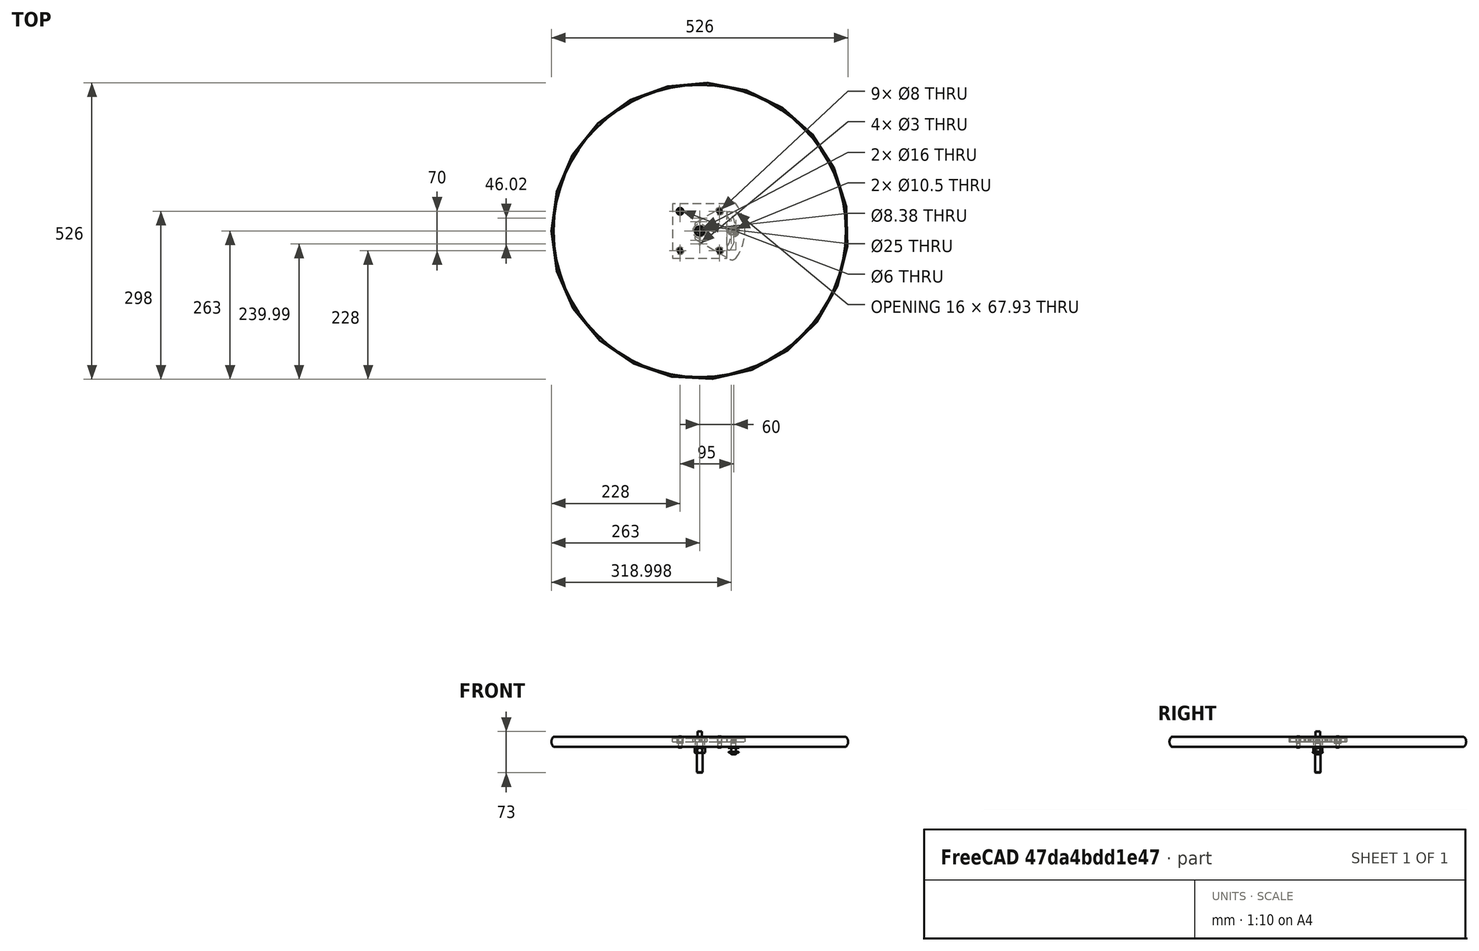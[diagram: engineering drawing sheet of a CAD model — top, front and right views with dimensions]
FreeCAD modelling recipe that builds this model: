
FCSTD DOCUMENT  (FreeCAD 0.19R24366 (Git))
Label: assembly
License: All rights reserved
LicenseURL: http://en.wikipedia.org/wiki/All_rights_reserved
objects: TechDraw::DrawViewDimension×16, Sketcher::SketchObject×14, Part::FeaturePython×13, PartDesign::Hole×8, App::FeaturePython×7, PartDesign::Body×6, App::Part×5, TechDraw::DrawViewPart×4, PartDesign::Revolution×3, PartDesign::Pad×3, PartDesign::Chamfer×1, TechDraw::DrawSVGTemplate×1, TechDraw::DrawRichAnno×1, TechDraw::DrawPage×1
note: 62 computed .brp shape members not serialized (recipe doc carries the construction recipe); baked Part::Feature solids carry a one-line shape summary decoded from their .brp

FEATURE [Sketcher::SketchObject] Sketch
  FullyConstrained = false
  MapMode = 5
  Placement = pos=(0,0,0) rot=(1,0,0;1.5708rad)
  Support = -> [XZ_Plane001]
  sketch-geometry (5):
    g0: LineSegment StartX=0 StartY=9 StartZ=0 EndX=-259 EndY=9 EndZ=0
    g1: LineSegment StartX=0 StartY=9 StartZ=0 EndX=0 EndY=-9 EndZ=0
    g2: LineSegment StartX=0 StartY=-9 StartZ=0 EndX=-259 EndY=-9 EndZ=0
    g3: ArcOfCircle CenterX=-250.875 CenterY=0 CenterZ=0 NormalX=0 NormalY=0 NormalZ=1 AngleXU=0 Radius=12.125 StartAngle=2.30514 EndAngle=3.97804
    g4: LineSegment StartX=-263 StartY=113.76 StartZ=0 EndX=-263 EndY=-132.948 EndZ=0
  constraints (14):
    c: PointOnObject(g0,g-2)
    c: Horizontal(g0)
    c: Coincident(g1,g0)
    c: Horizontal(g2)
    c: PointOnObject(g3,g-1)
    c: Coincident(g3,g0)
    c: Coincident(g3,g2)
    c: Symmetric(g1,g0,g-1)
    c: DistanceX(g0,g0) = 259
    c: Vertical(g4)
    c: DistanceX(g4,g-1) = 263
    c: Tangent(g3,g4)
    c: Coincident(g1,g2)
    c: DistanceY(g1,g1) = 18
FEATURE [PartDesign::Revolution] Revolution
  Angle = 360
  Axis = (0,2e-16,1)
  Base = (0,0,0)
  Placement = pos=(0,0,0) rot=(1,0,0;1.5708rad)
  Profile = -> Sketch
  ReferenceAxis = -> Sketch [V_Axis]
FEATURE [Sketcher::SketchObject] Sketch001
  FullyConstrained = false
  MapMode = 5
  Placement = pos=(0,4e-15,9) rot=(0,0,1;3.14159rad)
  Support = -> [Revolution]
  sketch-geometry (1):
    g0: Circle CenterX=0 CenterY=0 CenterZ=0 NormalX=0 NormalY=0 NormalZ=1 AngleXU=0 Radius=3.02563
  constraints (1):
    c: Coincident(g0,g-1)
FEATURE [PartDesign::Hole] Hole
  BaseFeature = -> Revolution
  Depth = 25
  DepthType = 0
  Diameter = 16
  DrillForDepth = false
  DrillPoint = 1
  DrillPointAngle = 118
  HoleCutCountersinkAngle = 90
  HoleCutCustomValues = false
  HoleCutDepth = 0
  HoleCutDiameter = 6.1
  HoleCutType = 0
  ModelActualThread = false
  Placement = pos=(0,0,0) rot=(1,0,0;1.5708rad)
  Profile = -> Sketch001
  Tapered = false
  TaperedAngle = 90
  ThreadAngle = 0
  ThreadClass = 0
  ThreadCutOffInner = 0
  ThreadCutOffOuter = 0
  ThreadDirection = 0
  ThreadFit = 0
  ThreadPitch = 0
  ThreadSize = 0
  ThreadType = 0
  Threaded = false
FEATURE [Sketcher::SketchObject] Sketch002
  FullyConstrained = true
  MapMode = 5
  Support = -> [XY_Plane003]
  sketch-geometry (4):
    g0: LineSegment StartX=-48.5 StartY=-48.5 StartZ=0 EndX=48.5 EndY=-48.5 EndZ=0
    g1: LineSegment StartX=48.5 StartY=-48.5 StartZ=0 EndX=48.5 EndY=48.5 EndZ=0
    g2: LineSegment StartX=48.5 StartY=48.5 StartZ=0 EndX=-48.5 EndY=48.5 EndZ=0
    g3: LineSegment StartX=-48.5 StartY=48.5 StartZ=0 EndX=-48.5 EndY=-48.5 EndZ=0
  constraints (11):
    c: Coincident(g0,g1)
    c: Coincident(g1,g2)
    c: Coincident(g2,g3)
    c: Coincident(g3,g0)
    c: Horizontal(g0)
    c: Horizontal(g2)
    c: Vertical(g1)
    c: Vertical(g3)
    c: Symmetric(g2,g0,g-1)
    c: Equal(g2,g1)
    c: DistanceX(g2,g2) = 97
FEATURE [PartDesign::Pad] Pad
  Direction = (1,1,1)
  Length = 6
  Length2 = 100
  Profile = -> Sketch002
  Type = 0
FEATURE [Sketcher::SketchObject] Sketch003
  FullyConstrained = false
  MapMode = 5
  Placement = pos=(0,0,6) rot=(0,0,1;0rad)
  Support = -> [Pad]
  sketch-geometry (6):
    g0: Circle CenterX=35 CenterY=35 CenterZ=0 NormalX=0 NormalY=0 NormalZ=1 AngleXU=0 Radius=3.3
    g1: Circle CenterX=35 CenterY=-35 CenterZ=0 NormalX=0 NormalY=0 NormalZ=1 AngleXU=0 Radius=3.3
    g2: Circle CenterX=-35 CenterY=35 CenterZ=0 NormalX=0 NormalY=0 NormalZ=1 AngleXU=0 Radius=3.3
    g3: Circle CenterX=-35 CenterY=-35 CenterZ=0 NormalX=0 NormalY=0 NormalZ=1 AngleXU=0 Radius=3.3
    g4: LineSegment StartX=-35 StartY=35 StartZ=0 EndX=35 EndY=35 EndZ=0
    g5: LineSegment StartX=35 StartY=35 StartZ=0 EndX=35 EndY=-35 EndZ=0
  constraints (9):
    c: Symmetric(g1,g2,g-1)
    c: Symmetric(g0,g3,g-1)
    c: Symmetric(g2,g0,g-2)
    c: Coincident(g4,g2)
    c: Coincident(g4,g0)
    c: DistanceX(g4,g4) = 70
    c: Coincident(g5,g4)
    c: Coincident(g5,g1)
    c: Equal(g4,g5)
FEATURE [PartDesign::Hole] Hole001
  BaseFeature = -> Pad
  Depth = 25
  DepthType = 0
  Diameter = 8
  DrillForDepth = false
  DrillPoint = 1
  DrillPointAngle = 118
  HoleCutCountersinkAngle = 90
  HoleCutCustomValues = false
  HoleCutDepth = 0
  HoleCutDiameter = 0
  HoleCutType = 0
  ModelActualThread = false
  Profile = -> Sketch003
  Tapered = false
  TaperedAngle = 90
  ThreadAngle = 0
  ThreadClass = 0
  ThreadCutOffInner = 0
  ThreadCutOffOuter = 0
  ThreadDirection = 0
  ThreadFit = 0
  ThreadPitch = 0
  ThreadSize = 0
  ThreadType = 0
  Threaded = false
FEATURE [Sketcher::SketchObject] Sketch004
  FullyConstrained = false
  MapMode = 5
  Placement = pos=(0,0,6) rot=(0,0,1;0rad)
  Support = -> [Hole001]
  sketch-geometry (1):
    g0: Circle CenterX=0 CenterY=0 CenterZ=0 NormalX=0 NormalY=0 NormalZ=1 AngleXU=0 Radius=7.11938
  constraints (1):
    c: Coincident(g0,g-1)
FEATURE [PartDesign::Hole] Hole002
  BaseFeature = -> Hole001
  Depth = 25
  DepthType = 0
  Diameter = 25
  DrillForDepth = false
  DrillPoint = 1
  DrillPointAngle = 118
  HoleCutCountersinkAngle = 90
  HoleCutCustomValues = false
  HoleCutDepth = 0
  HoleCutDiameter = 6.1
  HoleCutType = 0
  ModelActualThread = false
  Profile = -> Sketch004
  Tapered = false
  TaperedAngle = 90
  ThreadAngle = 0
  ThreadClass = 0
  ThreadCutOffInner = 0
  ThreadCutOffOuter = 0
  ThreadDirection = 0
  ThreadFit = 0
  ThreadPitch = 0
  ThreadSize = 0
  ThreadType = 0
  Threaded = false
  expr: Diameter = 2 * Sketch010.Constraints[16]
FEATURE [Sketcher::SketchObject] Sketch005
  FullyConstrained = false
  MapMode = 5
  Placement = pos=(0,0,6) rot=(0,0,1;0rad)
  Support = -> [Hole002]
  sketch-geometry (6):
    g0: Circle CenterX=0 CenterY=16.22 CenterZ=0 NormalX=0 NormalY=0 NormalZ=1 AngleXU=0 Radius=1.5917
    g1: Circle CenterX=0 CenterY=23.01 CenterZ=0 NormalX=0 NormalY=0 NormalZ=1 AngleXU=0 Radius=1.57748
    g2: Circle CenterX=0 CenterY=-16.22 CenterZ=0 NormalX=0 NormalY=0 NormalZ=1 AngleXU=0 Radius=1.5917
    g3: Circle CenterX=0 CenterY=-23.01 CenterZ=0 NormalX=0 NormalY=0 NormalZ=1 AngleXU=0 Radius=1.66102
    g4: Circle CenterX=0 CenterY=0 CenterZ=0 NormalX=0 NormalY=0 NormalZ=1 AngleXU=0 Radius=23.01
    g5: Circle CenterX=0 CenterY=0 CenterZ=0 NormalX=0 NormalY=0 NormalZ=1 AngleXU=0 Radius=16.22
  constraints (10):
    c: PointOnObject(g0,g-2)
    c: PointOnObject(g1,g-2)
    c: Symmetric(g0,g2,g-1)
    c: Symmetric(g3,g1,g-1)
    c: Coincident(g4,g-1)
    c: Diameter(g4) = 46.02
    c: PointOnObject(g1,g4)
    c: Coincident(g5,g-1)
    c: Diameter(g5) = 32.44
    c: PointOnObject(g0,g5)
FEATURE [PartDesign::Hole] Hole003
  BaseFeature = -> Hole002
  Depth = 25
  DepthType = 0
  Diameter = 3
  DrillForDepth = false
  DrillPoint = 1
  DrillPointAngle = 118
  HoleCutCountersinkAngle = 90
  HoleCutCustomValues = false
  HoleCutDepth = 0
  HoleCutDiameter = 6.1
  HoleCutType = 0
  ModelActualThread = false
  Profile = -> Sketch005
  Tapered = false
  TaperedAngle = 90
  ThreadAngle = 0
  ThreadClass = 0
  ThreadCutOffInner = 0
  ThreadCutOffOuter = 0
  ThreadDirection = 0
  ThreadFit = 0
  ThreadPitch = 0
  ThreadSize = 0
  ThreadType = 0
  Threaded = false
FEATURE [PartDesign::Body] Body001
  Group = -> [Sketch002,Pad,Sketch003,Hole001,Sketch004,Hole002,Sketch005,Hole003]
  Origin = -> Origin003
  Tip = -> Hole003
FEATURE [Sketcher::SketchObject] Sketch007
  FullyConstrained = false
  MapMode = 5
  Placement = pos=(0,0,0) rot=(1,0,0;1.5708rad)
  Support = -> [XZ_Plane005]
  sketch-geometry (5):
    g0: LineSegment StartX=0 StartY=9 StartZ=0 EndX=-259 EndY=9 EndZ=0
    g1: LineSegment StartX=0 StartY=9 StartZ=0 EndX=0 EndY=-9 EndZ=0
    g2: LineSegment StartX=0 StartY=-9 StartZ=0 EndX=-259 EndY=-9 EndZ=0
    g3: ArcOfCircle CenterX=-250.875 CenterY=0 CenterZ=0 NormalX=0 NormalY=0 NormalZ=1 AngleXU=0 Radius=12.125 StartAngle=2.30514 EndAngle=3.97804
    g4: LineSegment StartX=-263 StartY=113.76 StartZ=0 EndX=-263 EndY=-132.948 EndZ=0
  constraints (14):
    c: PointOnObject(g0,g-2)
    c: Horizontal(g0)
    c: Coincident(g1,g0)
    c: Horizontal(g2)
    c: PointOnObject(g3,g-1)
    c: Coincident(g3,g0)
    c: Coincident(g3,g2)
    c: Symmetric(g1,g0,g-1)
    c: DistanceX(g0,g0) = 259
    c: Vertical(g4)
    c: DistanceX(g4,g-1) = 263
    c: Tangent(g3,g4)
    c: Coincident(g1,g2)
    c: DistanceY(g1,g1) = 18
FEATURE [PartDesign::Revolution] Revolution001
  Angle = 360
  Axis = (0,2e-16,1)
  Base = (0,0,0)
  Placement = pos=(0,0,0) rot=(1,0,0;1.5708rad)
  Profile = -> Sketch007
  ReferenceAxis = -> Sketch007 [V_Axis]
FEATURE [Sketcher::SketchObject] Sketch008
  FullyConstrained = false
  MapMode = 5
  Placement = pos=(0,4e-15,9) rot=(0,0,1;3.14159rad)
  Support = -> [Revolution001]
  sketch-geometry (1):
    g0: Circle CenterX=0 CenterY=0 CenterZ=0 NormalX=0 NormalY=0 NormalZ=1 AngleXU=0 Radius=3.02563
  constraints (1):
    c: Coincident(g0,g-1)
FEATURE [PartDesign::Hole] Hole005
  BaseFeature = -> Revolution001
  Depth = 25
  DepthType = 0
  Diameter = 16
  DrillForDepth = false
  DrillPoint = 1
  DrillPointAngle = 118
  HoleCutCountersinkAngle = 90
  HoleCutCustomValues = false
  HoleCutDepth = 0
  HoleCutDiameter = 0
  HoleCutType = 0
  ModelActualThread = false
  Placement = pos=(0,0,0) rot=(1,0,0;1.5708rad)
  Profile = -> Sketch008
  Tapered = false
  TaperedAngle = 90
  ThreadAngle = 0
  ThreadClass = 0
  ThreadCutOffInner = 0
  ThreadCutOffOuter = 0
  ThreadDirection = 0
  ThreadFit = 0
  ThreadPitch = 0
  ThreadSize = 0
  ThreadType = 0
  Threaded = false
  expr: Diameter = Hole.Diameter
FEATURE [Sketcher::SketchObject] Sketch009
  FullyConstrained = false
  MapMode = 5
  Placement = pos=(0,4e-15,9) rot=(0,0,1;3.14159rad)
  Support = -> [Hole005]
  expr: Constraints[4] = Sketch003.Constraints[5]
  expr: Constraints[5] = Sketch003.Constraints[5]
  sketch-geometry (4):
    g0: Circle CenterX=-35 CenterY=35 CenterZ=0 NormalX=0 NormalY=0 NormalZ=1 AngleXU=0 Radius=2.46691
    g1: Circle CenterX=35 CenterY=35 CenterZ=0 NormalX=0 NormalY=0 NormalZ=1 AngleXU=0 Radius=2.46691
    g2: Circle CenterX=-35 CenterY=-35 CenterZ=0 NormalX=0 NormalY=0 NormalZ=1 AngleXU=0 Radius=2.46691
    g3: Circle CenterX=35 CenterY=-35 CenterZ=0 NormalX=0 NormalY=0 NormalZ=1 AngleXU=0 Radius=2.46691
  constraints (6):
    c: Symmetric(g0,g3,g-1)
    c: Symmetric(g1,g2,g-1)
    c: Vertical(g2,g0)
    c: Horizontal(g0,g1)
    c: DistanceY(g2,g0) = 70
    c: DistanceX(g2,g3) = 70
FEATURE [PartDesign::Hole] Hole006
  BaseFeature = -> Hole005
  Depth = 10
  DepthType = 0
  Diameter = 8
  DrillForDepth = false
  DrillPoint = 1
  DrillPointAngle = 118
  HoleCutCountersinkAngle = 90
  HoleCutCustomValues = false
  HoleCutDepth = 10.8
  HoleCutDiameter = 20.4
  HoleCutType = 0
  ModelActualThread = false
  Placement = pos=(0,0,0) rot=(1,0,0;1.5708rad)
  Profile = -> Sketch009
  Tapered = false
  TaperedAngle = 90
  ThreadAngle = 0
  ThreadClass = 0
  ThreadCutOffInner = 0
  ThreadCutOffOuter = 0
  ThreadDirection = 0
  ThreadFit = 0
  ThreadPitch = 0
  ThreadSize = 0
  ThreadType = 0
  Threaded = false
FEATURE [PartDesign::Body] Body002  label="Upper Plate"
  Group = -> [Sketch007,Revolution001,Sketch008,Hole005,Sketch009,Hole006]
  Origin = -> Origin005
  Tip = -> Hole006
FEATURE [Sketcher::SketchObject] Sketch010
  FullyConstrained = true
  MapMode = 5
  Placement = pos=(0,0,0) rot=(1,0,0;1.5708rad)
  Support = -> [XZ_Plane007]
  sketch-geometry (8):
    g0: LineSegment StartX=0 StartY=18 StartZ=0 EndX=-4 EndY=18 EndZ=0
    g1: LineSegment StartX=-4 StartY=18 StartZ=0 EndX=-4 EndY=5.5 EndZ=0
    g2: LineSegment StartX=-4 StartY=5.5 StartZ=0 EndX=-12.5 EndY=5.5 EndZ=0
    g3: LineSegment StartX=-12.5 StartY=5.5 StartZ=0 EndX=-12.5 EndY=0 EndZ=0
    g4: LineSegment StartX=-12.5 StartY=0 StartZ=0 EndX=-5 EndY=0 EndZ=0
    g5: LineSegment StartX=-5 StartY=0 StartZ=0 EndX=-5 EndY=-55 EndZ=0
    g6: LineSegment StartX=-5 StartY=-55 StartZ=0 EndX=0 EndY=-55 EndZ=0
    g7: LineSegment StartX=0 StartY=18 StartZ=0 EndX=0 EndY=-55 EndZ=0
  constraints (23):
    c: PointOnObject(g0,g-2)
    c: Coincident(g1,g0)
    c: Vertical(g1)
    c: Coincident(g2,g1)
    c: Horizontal(g2)
    c: Coincident(g3,g2)
    c: Coincident(g4,g3)
    c: Vertical(g5)
    c: Coincident(g6,g5)
    c: PointOnObject(g6,g-2)
    c: Tangent(g4,g-1)
    c: Coincident(g4,g5)
    c: Vertical(g3)
    c: Horizontal(g0)
    c: Horizontal(g6)
    c: DistanceX(g0,g0) = 4
    c: DistanceX(g3,g-1) = 12.5
    c: DistanceY(g3,g3) = 5.5
    c: DistanceY(g1,g1) = 12.5
    c: DistanceX(g6,g6) = 5
    c: Coincident(g7,g0)
    c: Coincident(g7,g6)
    c: DistanceY(g7,g7) = 73
FEATURE [PartDesign::Revolution] Revolution002
  Angle = 360
  Axis = (0,2e-16,1)
  Base = (0,0,0)
  Placement = pos=(0,0,0) rot=(1,0,0;1.5708rad)
  Profile = -> Sketch010
  ReferenceAxis = -> Sketch010 [V_Axis]
FEATURE [Part::FeaturePython] Screw  label="M6x16-Screw"  # Fasteners workbench fastener (typed FeaturePython)
  Placement = pos=(-35,35,6) rot=(0,0,1;0rad)
  baseObject = -> Body001 [Edge26]
  diameter = 4
  invert = false
  length = 3
  lengthCustom = 16
  matchOuter = false
  offset = 0
  thread = false
  type = 41
FEATURE [Part::FeaturePython] Screw001  label="M6x16-Screw007"  # Fasteners workbench fastener (typed FeaturePython)
  Placement = pos=(35,35,6) rot=(0,0,1;0rad)
  baseObject = -> Body001 [Edge30]
  diameter = 4
  invert = false
  length = 3
  lengthCustom = 16
  matchOuter = false
  offset = 0
  thread = false
  type = 41
FEATURE [Part::FeaturePython] Screw002  label="M6x16-Screw008"  # Fasteners workbench fastener (typed FeaturePython)
  Placement = pos=(-35,-35,6) rot=(0,0,1;0rad)
  baseObject = -> Body001 [Edge22]
  diameter = 4
  invert = false
  length = 3
  lengthCustom = 16
  matchOuter = false
  offset = 0
  thread = false
  type = 41
FEATURE [Part::FeaturePython] Screw003  label="M6x16-Screw009"  # Fasteners workbench fastener (typed FeaturePython)
  Placement = pos=(35,-35,6) rot=(0,0,1;0rad)
  baseObject = -> Body001 [Edge24]
  diameter = 4
  invert = false
  length = 3
  lengthCustom = 16
  matchOuter = false
  offset = 0
  thread = false
  type = 41
FEATURE [App::Part] Part001  label="Sensor Plate"
  Group = -> [Body001,Screw,Screw001,Screw002,Screw003]
  Origin = -> Origin002
  Placement = pos=(0,0,30) rot=(0,0,1;0rad)
FEATURE [Sketcher::SketchObject] Sketch011
  FullyConstrained = true
  MapMode = 5
  Support = -> [XY_Plane008]
  expr: Constraints[12] = Sketch003.Constraints[5]
  expr: Constraints[13] = Sketch003.Constraints[5]
  sketch-geometry (6):
    g0: Circle CenterX=-35 CenterY=35 CenterZ=0 NormalX=0 NormalY=0 NormalZ=1 AngleXU=0 Radius=6
    g1: Circle CenterX=35 CenterY=35 CenterZ=0 NormalX=0 NormalY=0 NormalZ=1 AngleXU=0 Radius=6
    g2: Circle CenterX=-35 CenterY=-35 CenterZ=0 NormalX=0 NormalY=0 NormalZ=1 AngleXU=0 Radius=6
    g3: Circle CenterX=35 CenterY=-35 CenterZ=0 NormalX=0 NormalY=0 NormalZ=1 AngleXU=0 Radius=6
    g4: LineSegment StartX=-35 StartY=-35 StartZ=0 EndX=35 EndY=-35 EndZ=0
    g5: LineSegment StartX=-35 StartY=35 StartZ=0 EndX=-35 EndY=-35 EndZ=0
  constraints (14):
    c: Diameter(g0) = 12
    c: Equal(g0,g1)
    c: Equal(g1,g3)
    c: Equal(g3,g2)
    c: Symmetric(g0,g3,g-1)
    c: Symmetric(g2,g1,g-1)
    c: Horizontal(g0,g1)
    c: Vertical(g2,g0)
    c: Coincident(g4,g2)
    c: Coincident(g4,g3)
    c: Coincident(g5,g0)
    c: Coincident(g5,g4)
    c: DistanceY(g5,g5) = 70
    c: DistanceX(g4,g4) = 70
FEATURE [PartDesign::Pad] Pad001
  Direction = (1,1,1)
  Length = 12
  Length2 = 100
  Profile = -> Sketch011
  Type = 0
FEATURE [Sketcher::SketchObject] Sketch012
  ExternalGeometry = -> [Sketch011]
  FullyConstrained = false
  MapMode = 5
  Placement = pos=(0,0,12) rot=(0,0,1;0rad)
  Support = -> [Pad001]
  sketch-geometry (1):
    g0: Circle CenterX=-35 CenterY=35 CenterZ=0 NormalX=0 NormalY=0 NormalZ=1 AngleXU=0 Radius=3.67821
  constraints (1):
    c: Coincident(g0,g-3)
FEATURE [PartDesign::Hole] Hole007
  BaseFeature = -> Pad001
  Depth = 25
  DepthType = 0
  Diameter = 6
  DrillForDepth = false
  DrillPoint = 1
  DrillPointAngle = 118
  HoleCutCountersinkAngle = 90
  HoleCutCustomValues = false
  HoleCutDepth = 0
  HoleCutDiameter = 6.1
  HoleCutType = 0
  ModelActualThread = false
  Profile = -> Sketch012
  Tapered = false
  TaperedAngle = 90
  ThreadAngle = 0
  ThreadClass = 0
  ThreadCutOffInner = 0
  ThreadCutOffOuter = 0
  ThreadDirection = 0
  ThreadFit = 0
  ThreadPitch = 0
  ThreadSize = 0
  ThreadType = 0
  Threaded = false
FEATURE [PartDesign::Body] Body004
  Group = -> [Sketch011,Pad001,Sketch012,Hole007]
  Origin = -> Origin008
  Placement = pos=(0,0,-3) rot=(0,0,1;0rad)
  Tip = -> Hole007
FEATURE [App::Part] Part002  label="Upper Base Plate"
  Group = -> [Body002,Body004]
  Origin = -> Origin004
  Placement = pos=(0,0,21) rot=(0,0,1;0rad)
FEATURE [Sketcher::SketchObject] Sketch013
  FullyConstrained = false
  MapMode = 5
  Support = -> [XY_Plane010]
  sketch-geometry (22):
    g0: LineSegment StartX=9.2376 StartY=0 StartZ=0 EndX=4.6188 EndY=8 EndZ=0
    g1: LineSegment StartX=4.6188 StartY=8 StartZ=0 EndX=-4.6188 EndY=8 EndZ=0
    g2: LineSegment StartX=-4.6188 StartY=-8 StartZ=0 EndX=4.6188 EndY=-8 EndZ=0
    g3: LineSegment StartX=4.6188 StartY=-8 StartZ=0 EndX=9.2376 EndY=0 EndZ=0
    g4: Circle CenterX=0 CenterY=0 CenterZ=0 NormalX=0 NormalY=0 NormalZ=1 AngleXU=0 Radius=9.2376
    g5: ArcOfCircle CenterX=-4.6188 CenterY=12 CenterZ=0 NormalX=0 NormalY=0 NormalZ=1 AngleXU=0 Radius=4 StartAngle=2.0944 EndAngle=4.71239
    g6: LineSegment StartX=-6.6188 StartY=15.4641 StartZ=0 EndX=53.5459 EndY=50.2002 EndZ=0
    g7: ArcOfCircle CenterX=57.5459 CenterY=43.272 CenterZ=0 NormalX=0 NormalY=0 NormalZ=1 AngleXU=0 Radius=8 StartAngle=0.644752 EndAngle=2.0944
    g8: ArcOfCircle CenterX=0 CenterY=0 CenterZ=0 NormalX=0 NormalY=0 NormalZ=1 AngleXU=0 Radius=80 StartAngle=5.63843 EndAngle=6.92794
    g9: ArcOfCircle CenterX=57.5459 CenterY=-43.272 CenterZ=0 NormalX=0 NormalY=0 NormalZ=1 AngleXU=0 Radius=8 StartAngle=4.18879 EndAngle=5.63843
    g10: LineSegment StartX=-6.6188 StartY=-15.4641 StartZ=0 EndX=53.5459 EndY=-50.2002 EndZ=0
    g11: ArcOfCircle CenterX=0 CenterY=0 CenterZ=0 NormalX=0 NormalY=0 NormalZ=1 AngleXU=0 Radius=64 StartAngle=5.75959 EndAngle=6.80678
    g12: ArcOfCircle CenterX=0 CenterY=0 CenterZ=0 NormalX=0 NormalY=0 NormalZ=1 AngleXU=0 Radius=56 StartAngle=5.75959 EndAngle=6.80678
    g13: ArcOfCircle CenterX=51.9615 CenterY=30 CenterZ=0 NormalX=0 NormalY=0 NormalZ=1 AngleXU=0 Radius=4 StartAngle=0.523599 EndAngle=3.66519
    g14: ArcOfCircle CenterX=51.9615 CenterY=-30 CenterZ=0 NormalX=0 NormalY=0 NormalZ=1 AngleXU=0 Radius=4 StartAngle=2.61799 EndAngle=5.75959
    g15: Circle CenterX=0 CenterY=0 CenterZ=0 NormalX=0 NormalY=0 NormalZ=1 AngleXU=0 Radius=60
    g16: LineSegment StartX=0 StartY=0 StartZ=0 EndX=105.295 EndY=60.7919 EndZ=0
    g17: LineSegment StartX=0 StartY=0 StartZ=0 EndX=105.295 EndY=-60.7919 EndZ=0
    g18: GeomPoint X=51.9615 Y=-30 Z=0
    g19: ArcOfCircle CenterX=-4.6188 CenterY=-12 CenterZ=0 NormalX=0 NormalY=0 NormalZ=1 AngleXU=0 Radius=4 StartAngle=1.5708 EndAngle=4.18879
    g20: GeomPoint X=0 Y=8 Z=0
    g21: Circle CenterX=0 CenterY=0 CenterZ=0 NormalX=0 NormalY=0 NormalZ=1 AngleXU=0 Radius=8
  constraints (52):
    c: Coincident(g0,g1)
    c: Coincident(g2,g3)
    c: Coincident(g3,g0)
    c: Equal(g0,g1)
    c: Equal(g0,g2)
    c: Equal(g0,g3)
    c: PointOnObject(g0,g4)
    c: PointOnObject(g1,g4)
    c: PointOnObject(g2,g4)
    c: PointOnObject(g2,g4)
    c: PointOnObject(g3,g4)
    c: Coincident(g4,g-1)
    c: PointOnObject(g3,g-1)
    c: DistanceY(g2,g1) = 16
    c: Horizontal(g1)
    c: Coincident(g4,g8)
    c: Coincident(g11,g-1)
    c: Coincident(g12,g-1)
    c: Coincident(g15,g-1)
    c: PointOnObject(g13,g15)
    c: Diameter(g13) = 8
    c: Tangent(g13,g12) = 1.5708
    c: Tangent(g13,g11) = -1.5708
    c: Tangent(g14,g11) = -1.5708
    c: Tangent(g14,g12) = 1.5708
    c: Coincident(g16,g-1)
    c: Coincident(g17,g-1)
    c: Symmetric(g17,g16,g-1)
    c: Angle(g17,g16) = 1.0472
    c: PointOnObject(g18,g17)
    c: Coincident(g18,g14)
    c: PointOnObject(g13,g16)
    c: Radius(g15) = 60
    c: Parallel(g17,g10)
    c: Radius(g8) = 80
    c: Parallel(g16,g6)
    c: Tangent(g5,g1) = 1.5708
    c: Tangent(g6,g5) = 1.5708
    c: Tangent(g19,g2) = 1.5708
    c: Tangent(g19,g10) = -1.5708
    c: Tangent(g8,g7) = -1.5708
    c: Tangent(g9,g8) = -1.5708
    c: Tangent(g7,g6) = 1.5708
    c: Tangent(g10,g9) = -1.5708
    c: Equal(g19,g5)
    c: Radius(g5) = 4
    c: PointOnObject(g20,g1)
    c: PointOnObject(g20,g-2)
    c: Coincident(g21,g-1)
    c: PointOnObject(g20,g21)
    c: Equal(g7,g9)
    c: Radius(g7) = 8
FEATURE [PartDesign::Pad] Pad002
  Direction = (1,1,1)
  Length = 6
  Length2 = 100
  Profile = -> Sketch013
  Type = 0
FEATURE [PartDesign::Body] Body005
  Group = -> [Sketch013,Pad002]
  Origin = -> Origin010
  Tip = -> Pad002
FEATURE [App::Part] Part004  label="Clamp"
  Group = -> [Body005]
  Origin = -> Origin009
  Placement = pos=(0,0,-18) rot=(0,0,1;0rad)
FEATURE [Part::FeaturePython] Washer  label="M10-Washer"  # Fasteners workbench fastener (typed FeaturePython)
  Placement = pos=(0,-6e-15,-9) rot=(1,0,0;3.14159rad)
  baseObject = -> Body [Edge6]
  diameter = 9
  invert = false
  matchOuter = false
  offset = 0
  type = 3
FEATURE [Part::FeaturePython] Nut  label="M10-Nut"  # Fasteners workbench fastener (typed FeaturePython)
  Placement = pos=(0,-6e-15,-11.2) rot=(1,0,0;3.14159rad)
  baseObject = -> Washer [Edge1]
  diameter = 10
  invert = false
  matchOuter = false
  offset = 0
  thread = false
  type = 7
FEATURE [PartDesign::Chamfer] Chamfer
  Angle = 45
  Base = -> Revolution002 [Edge8]
  BaseFeature = -> Revolution002
  ChamferType = 0
  FlipDirection = false
  Placement = pos=(0,0,0) rot=(1,0,0;1.5708rad)
  Size = 1
  Size2 = 1
  SupportTransform = false
FEATURE [PartDesign::Body] Body003
  Group = -> [Sketch010,Revolution002,Chamfer]
  Origin = -> Origin007
  Tip = -> Chamfer
FEATURE [App::Part] Part003  label="Bolt"
  Group = -> [Body003]
  Origin = -> Origin006
  Placement = pos=(0,0,30) rot=(0,0,1;0rad)
FEATURE [Sketcher::SketchObject] Sketch014
  FullyConstrained = false
  MapMode = 5
  Placement = pos=(0,-4e-15,-9) rot=(1,0,0;3.14159rad)
  Support = -> [Hole]
  expr: Constraints[1] = Sketch013.Constraints[32]
  sketch-geometry (1):
    g0: Circle CenterX=60 CenterY=0 CenterZ=0 NormalX=0 NormalY=0 NormalZ=1 AngleXU=0 Radius=9.13356
  constraints (2):
    c: PointOnObject(g0,g-1)
    c: DistanceX(g-1,g0) = 60
FEATURE [PartDesign::Hole] Hole008
  BaseFeature = -> Hole
  Depth = 12
  DepthType = 0
  Diameter = 8
  DrillForDepth = false
  DrillPoint = 1
  DrillPointAngle = 118
  HoleCutCountersinkAngle = 90
  HoleCutCustomValues = false
  HoleCutDepth = 0
  HoleCutDiameter = 6.1
  HoleCutType = 0
  ModelActualThread = false
  Placement = pos=(0,0,0) rot=(1,0,0;1.5708rad)
  Profile = -> Sketch014
  Tapered = false
  TaperedAngle = 90
  ThreadAngle = 0
  ThreadClass = 0
  ThreadCutOffInner = 0
  ThreadCutOffOuter = 0
  ThreadDirection = 0
  ThreadFit = 0
  ThreadPitch = 0
  ThreadSize = 0
  ThreadType = 0
  Threaded = false
FEATURE [PartDesign::Body] Body
  Group = -> [Sketch,Revolution,Sketch001,Hole,Sketch014,Hole008]
  Origin = -> Origin001
  Tip = -> Hole008
FEATURE [App::Part] Part  label="Lower Base Plate"
  Group = -> [Body,Washer,Nut]
  Origin = -> Origin
FEATURE [Part::FeaturePython] Screw004  label="M8x16-Screw"  # Fasteners workbench fastener (typed FeaturePython)
  Placement = pos=(60,-8e-15,-18) rot=(1,0,0;3.14159rad)
  diameter = 5
  invert = false
  length = 2
  lengthCustom = 16
  matchOuter = false
  offset = 0
  thread = false
  type = 41
FEATURE [Part::FeaturePython] Washer001  label="M10-Washer001"  # Fasteners workbench fastener (typed FeaturePython)
  Placement = pos=(60,-5e-15,-9) rot=(1,0,0;3.14159rad)
  baseObject = -> Body [Edge7]
  diameter = 9
  invert = false
  matchOuter = false
  offset = 0
  type = 3
FEATURE [Part::FeaturePython] Parts  # WARN: FeaturePython — macro-defined, semantics opaque (R4)
  Group = -> [Screw004,Part004,Washer001]
  GroupMode = 0
FEATURE [TechDraw::DrawSVGTemplate] Template
  EditableTexts = AuthorName=AUTHOR NAME; CheckDate=CHECK DATE; CreationDate=CREATION DATE; DrawingNumber=NUMBER; FC-Scale=SCALE; FC-Title=TITLE; SheetNumber=SHEET; Subtitle=SUBTITLE; SupervisorName=SUPERVISOR NAME; Weight=WEIGHT
  Height = 297
  Orientation = 1
  Width = 420
FEATURE [TechDraw::DrawViewPart] View001
  CoarseView = false
  Direction = (0,-1,0)
  Focus = 100
  HardHidden = false
  IsoCount = 0
  IsoHidden = false
  IsoVisible = false
  LockPosition = false
  Perspective = false
  Rotation = 0
  ScaleType = 0
  SeamHidden = false
  SeamVisible = true
  SmoothHidden = false
  SmoothVisible = true
  Source = -> [Body003]
  X = 213.319
  XDirection = (1,0,0)
  Y = 193.091
FEATURE [TechDraw::DrawViewPart] View
  CoarseView = false
  Direction = (0,0,1)
  Focus = 100
  HardHidden = false
  IsoCount = 0
  IsoHidden = false
  IsoVisible = false
  LockPosition = false
  Perspective = false
  Rotation = 0
  ScaleType = 0
  SeamHidden = false
  SeamVisible = true
  SmoothHidden = false
  SmoothVisible = true
  Source = -> [Body001]
  X = 92.4337
  XDirection = (1,0,0)
  Y = 212.141
FEATURE [TechDraw::DrawViewDimension] Dimension004
  Arbitrary = false
  ArbitraryTolerances = false
  EqualTolerance = true
  FormatSpec = %.1f
  FormatSpecOverTolerance = %+.1f
  FormatSpecUnderTolerance = %+.1f
  Inverted = false
  LockPosition = false
  MeasureType = 1
  OverTolerance = 0
  References2D = -> [View]
  Rotation = 0
  ScaleType = 0
  TheoreticalExact = false
  Type = 1
  UnderTolerance = 0
  X = 0.930958
  Y = 57.251
FEATURE [TechDraw::DrawViewDimension] Dimension001
  Arbitrary = false
  ArbitraryTolerances = false
  EqualTolerance = true
  FormatSpec = ⌀%.1f
  FormatSpecOverTolerance = %+.1f
  FormatSpecUnderTolerance = %+.1f
  Inverted = false
  LockPosition = false
  MeasureType = 1
  OverTolerance = 0
  References2D = -> [View]
  Rotation = 0
  ScaleType = 0
  TheoreticalExact = false
  Type = 5
  UnderTolerance = 0
  X = -18.9295
  Y = 38.9451
FEATURE [TechDraw::DrawViewDimension] Dimension
  Arbitrary = false
  ArbitraryTolerances = false
  EqualTolerance = true
  FormatSpec = ⌀%.1f
  FormatSpecOverTolerance = %+.1f
  FormatSpecUnderTolerance = %+.1f
  Inverted = false
  LockPosition = false
  MeasureType = 1
  OverTolerance = 0
  References2D = -> [View]
  Rotation = 0
  ScaleType = 0
  TheoreticalExact = false
  Type = 5
  UnderTolerance = 0
  X = 4.20977
  Y = 3.88458
FEATURE [TechDraw::DrawViewDimension] Dimension005
  Arbitrary = false
  ArbitraryTolerances = false
  EqualTolerance = true
  FormatSpec = %.1f
  FormatSpecOverTolerance = %+.1f
  FormatSpecUnderTolerance = %+.1f
  Inverted = false
  LockPosition = false
  MeasureType = 1
  OverTolerance = 0
  References2D = -> [View]
  Rotation = 0
  ScaleType = 0
  TheoreticalExact = false
  Type = 2
  UnderTolerance = 0
  X = -56.32
  Y = 0
FEATURE [TechDraw::DrawViewDimension] Dimension002
  Arbitrary = false
  ArbitraryTolerances = false
  EqualTolerance = true
  FormatSpec = ⌀%.1f
  FormatSpecOverTolerance = %+.1f
  FormatSpecUnderTolerance = %+.1f
  Inverted = false
  LockPosition = false
  MeasureType = 1
  OverTolerance = 0
  References2D = -> [View]
  Rotation = 0
  ScaleType = 0
  TheoreticalExact = false
  Type = 5
  UnderTolerance = 0
  X = 13.6723
  Y = 26.8527
FEATURE [TechDraw::DrawViewPart] View002
  CoarseView = false
  Direction = (0,0,1)
  Focus = 100
  HardHidden = false
  IsoCount = 0
  IsoHidden = false
  IsoVisible = false
  LockPosition = false
  Perspective = false
  Rotation = 0
  ScaleType = 0
  SeamHidden = false
  SeamVisible = true
  SmoothHidden = false
  SmoothVisible = true
  Source = -> [Part003]
  X = 213.36
  XDirection = (1,0,0)
  Y = 256.023
FEATURE [TechDraw::DrawViewDimension] Dimension006
  Arbitrary = false
  ArbitraryTolerances = false
  EqualTolerance = true
  FormatSpec = ⌀%.1f
  FormatSpecOverTolerance = %+.1f
  FormatSpecUnderTolerance = %+.1f
  Inverted = false
  LockPosition = false
  MeasureType = 1
  OverTolerance = 0
  References2D = -> [View002]
  Rotation = 0
  ScaleType = 0
  TheoreticalExact = false
  Type = 5
  UnderTolerance = 0
  X = 25.2914
  Y = 4.07925
FEATURE [TechDraw::DrawViewDimension] Dimension007
  Arbitrary = false
  ArbitraryTolerances = false
  EqualTolerance = true
  FormatSpec = ⌀%.1f
  FormatSpecOverTolerance = %+.1f
  FormatSpecUnderTolerance = %+.1f
  Inverted = false
  LockPosition = false
  MeasureType = 1
  OverTolerance = 0
  References2D = -> [View002]
  Rotation = 0
  ScaleType = 0
  TheoreticalExact = false
  Type = 5
  UnderTolerance = 0
  X = 12.994
  Y = 15.6257
FEATURE [TechDraw::DrawViewDimension] Dimension008
  Arbitrary = false
  ArbitraryTolerances = false
  EqualTolerance = true
  FormatSpec = %.1f
  FormatSpecOverTolerance = %+.1f
  FormatSpecUnderTolerance = %+.1f
  Inverted = false
  LockPosition = false
  MeasureType = 1
  OverTolerance = 0
  References2D = -> [View001]
  Rotation = 0
  ScaleType = 0
  TheoreticalExact = false
  Type = 2
  UnderTolerance = 0
  X = 26.028
  Y = -1.42774
FEATURE [TechDraw::DrawViewDimension] Dimension009
  Arbitrary = false
  ArbitraryTolerances = false
  EqualTolerance = true
  FormatSpec = %.1f
  FormatSpecOverTolerance = %+.1f
  FormatSpecUnderTolerance = %+.1f
  Inverted = false
  LockPosition = false
  MeasureType = 1
  OverTolerance = 0
  References2D = -> [View001]
  Rotation = 0
  ScaleType = 0
  TheoreticalExact = false
  Type = 2
  UnderTolerance = 0
  X = 18.028
  Y = 16.3805
FEATURE [TechDraw::DrawViewDimension] Dimension010
  Arbitrary = false
  ArbitraryTolerances = false
  EqualTolerance = true
  FormatSpec = %.1f
  FormatSpecOverTolerance = %+.1f
  FormatSpecUnderTolerance = %+.1f
  Inverted = false
  LockPosition = false
  MeasureType = 1
  OverTolerance = 0
  References2D = -> [View001]
  Rotation = 0
  ScaleType = 0
  TheoreticalExact = false
  Type = 2
  UnderTolerance = 0
  X = -20.0466
  Y = 36.1393
FEATURE [TechDraw::DrawViewDimension] Dimension011
  Arbitrary = false
  ArbitraryTolerances = false
  EqualTolerance = true
  FormatSpec = %.1f
  FormatSpecOverTolerance = %+.1f
  FormatSpecUnderTolerance = %+.1f
  Inverted = false
  LockPosition = false
  MeasureType = 1
  OverTolerance = 0
  References2D = -> [View001]
  Rotation = 0
  ScaleType = 0
  TheoreticalExact = false
  Type = 2
  UnderTolerance = 0
  X = -11.9347
  Y = -8.70396
FEATURE [TechDraw::DrawViewPart] View003
  CoarseView = false
  Direction = (0,0,1)
  Focus = 100
  HardHidden = false
  IsoCount = 0
  IsoHidden = false
  IsoVisible = false
  LockPosition = false
  Perspective = false
  Rotation = 0
  ScaleType = 0
  SeamHidden = false
  SeamVisible = true
  SmoothHidden = false
  SmoothVisible = true
  Source = -> [Part004]
  X = 329.902
  XDirection = (1,0,0)
  Y = 213.323
FEATURE [TechDraw::DrawViewDimension] Dimension012
  Arbitrary = false
  ArbitraryTolerances = false
  EqualTolerance = true
  FormatSpec = R%.1f
  FormatSpecOverTolerance = %+.1f
  FormatSpecUnderTolerance = %+.1f
  Inverted = false
  LockPosition = false
  MeasureType = 1
  OverTolerance = 0
  References2D = -> [View003]
  Rotation = 0
  ScaleType = 0
  TheoreticalExact = false
  Type = 4
  UnderTolerance = 0
  X = 55.0932
  Y = 13.6151
FEATURE [TechDraw::DrawViewDimension] Dimension013
  Arbitrary = false
  ArbitraryTolerances = false
  EqualTolerance = true
  FormatSpec = %.1f
  FormatSpecOverTolerance = %+.1f
  FormatSpecUnderTolerance = %+.1f
  Inverted = false
  LockPosition = false
  MeasureType = 1
  OverTolerance = 0
  References2D = -> [View003]
  Rotation = 0
  ScaleType = 0
  TheoreticalExact = false
  Type = 2
  UnderTolerance = 0
  X = -48.8228
  Y = 0.681071
FEATURE [TechDraw::DrawViewDimension] Dimension014
  Arbitrary = false
  ArbitraryTolerances = false
  EqualTolerance = true
  FormatSpec = ⌀%.1f
  FormatSpecOverTolerance = %+.1f
  FormatSpecUnderTolerance = %+.1f
  Inverted = false
  LockPosition = false
  MeasureType = 1
  OverTolerance = 0
  References2D = -> [View003]
  Rotation = 0
  ScaleType = 0
  TheoreticalExact = false
  Type = 5
  UnderTolerance = 0
  X = 0.681071
  Y = 26.2212
FEATURE [TechDraw::DrawViewDimension] Dimension015
  Arbitrary = false
  ArbitraryTolerances = false
  EqualTolerance = true
  FormatSpec = R%.1f
  FormatSpecOverTolerance = %+.1f
  FormatSpecUnderTolerance = %+.1f
  Inverted = false
  LockPosition = false
  MeasureType = 1
  OverTolerance = 0
  References2D = -> [View003]
  Rotation = 0
  ScaleType = 0
  TheoreticalExact = false
  Type = 4
  UnderTolerance = 0
  X = 1.70268
  Y = -4.08643
FEATURE [TechDraw::DrawViewDimension] Dimension016
  Arbitrary = false
  ArbitraryTolerances = false
  EqualTolerance = true
  FormatSpec = R%.1f
  FormatSpecOverTolerance = %+.1f
  FormatSpecUnderTolerance = %+.1f
  Inverted = false
  LockPosition = false
  MeasureType = 1
  OverTolerance = 0
  References2D = -> [View003]
  Rotation = 0
  ScaleType = 0
  TheoreticalExact = false
  Type = 4
  UnderTolerance = 0
  X = -1.19187
  Y = -11.4079
FEATURE [TechDraw::DrawRichAnno] RichTextAnnotation
  AnnoText = <!DOCTYPE HTML PUBLIC "-//W3C//DTD HTML 4.0//EN" "http://www.w3.org/TR/REC-html40/strict.dtd">\n<html><head><meta name="qrichtext" content="1" /><style type="text/css">\np, li { white-space: pre-wrap; }\n</style></head><body style=" font-family:'Sans Serif'; font-size:9pt; font-weight:400; font-style:normal;">\n<p style=" margin-top:0px; margin-bottom:0px; margin-left:0px; margin-right:0px; -qt-block-indent:0; text-indent:0px;"><span style=" font-size:10pt;">t=6mm</span></p></body></html>
  LockPosition = false
  MaxWidth = -1
  Rotation = 0
  ScaleType = 0
  ShowFrame = true
  X = 120.883
  Y = 195.576
FEATURE [TechDraw::DrawPage] Page
  KeepUpdated = true
  NextBalloonIndex = 1
  ProjectionType = 0
  Template = -> Template
  Views = -> [View,Dimension,Dimension001,Dimension002,Dimension004,Dimension005,View001,View002,Dimension006,Dimension007,Dimension008,Dimension009,Dimension010,Dimension011,View003,Dimension012,Dimension013,Dimension014,Dimension015,Dimension016,RichTextAnnotation]
FEATURE [Part::FeaturePython] Assembly  # WARN: FeaturePython — macro-defined, semantics opaque (R4)
  AutoRelax = true
  BuildShape = 0
  Freeze = false
  Group = -> [Constraints,Elements,Parts]
  Verbose = false
  _SolverType = 1
  _Version = 1
FEATURE [App::FeaturePython] Constraints  # WARN: FeaturePython — macro-defined, semantics opaque (R4)
  Group = -> [Constraint,Constraint001]
  _Version = 1
FEATURE [App::FeaturePython] Elements  # WARN: FeaturePython — macro-defined, semantics opaque (R4)
  Group = -> [_Element,_Element001,_Element002]
FEATURE [Part::FeaturePython] _Element  # link proxy (typed FeaturePython)
  Detach = false
  LinkTransform = true
  LinkedObject = -> Screw004 [Face4]
  _Parent = -> Elements
FEATURE [Part::FeaturePython] _Element001  # link proxy (typed FeaturePython)
  Detach = false
  LinkTransform = true
  LinkedObject = -> Part004 [Body005.Pad002.Face16]
  _Parent = -> Elements
FEATURE [App::FeaturePython] Constraint  label="PlaneAlignment"  # WARN: FeaturePython — macro-defined, semantics opaque (R4)
  Angle = 0
  AnglePitch = 0
  AngleRoll = 0
  Cascade = false
  Disabled = false
  Group = -> [ElementLink,ElementLink001]
  LockAngle = false
  _ConstraintType = 37
  _Parent = -> Constraints
FEATURE [App::FeaturePython] ElementLink  label="_Element"  # link proxy (typed FeaturePython)
  LinkTransform = true
  LinkedObject = -> _Element
  _Parent = -> Constraint
FEATURE [App::FeaturePython] ElementLink001  label="_Element001"  # link proxy (typed FeaturePython)
  LinkTransform = true
  LinkedObject = -> _Element001
  _Parent = -> Constraint
FEATURE [App::FeaturePython] Constraint001  label="Locked"  # WARN: FeaturePython — macro-defined, semantics opaque (R4)
  Disabled = false
  Group = -> [ElementLink002]
  _ConstraintType = 0
  _Parent = -> Constraints
FEATURE [App::FeaturePython] ElementLink002  label="_Element002"  # link proxy (typed FeaturePython)
  LinkTransform = true
  LinkedObject = -> _Element002
  _Parent = -> Constraint001
FEATURE [Part::FeaturePython] _Element002  # link proxy (typed FeaturePython)
  Detach = false
  LinkTransform = true
  LinkedObject = -> Part004 [Body005.Pad002.Face17]
  _Parent = -> Elements
